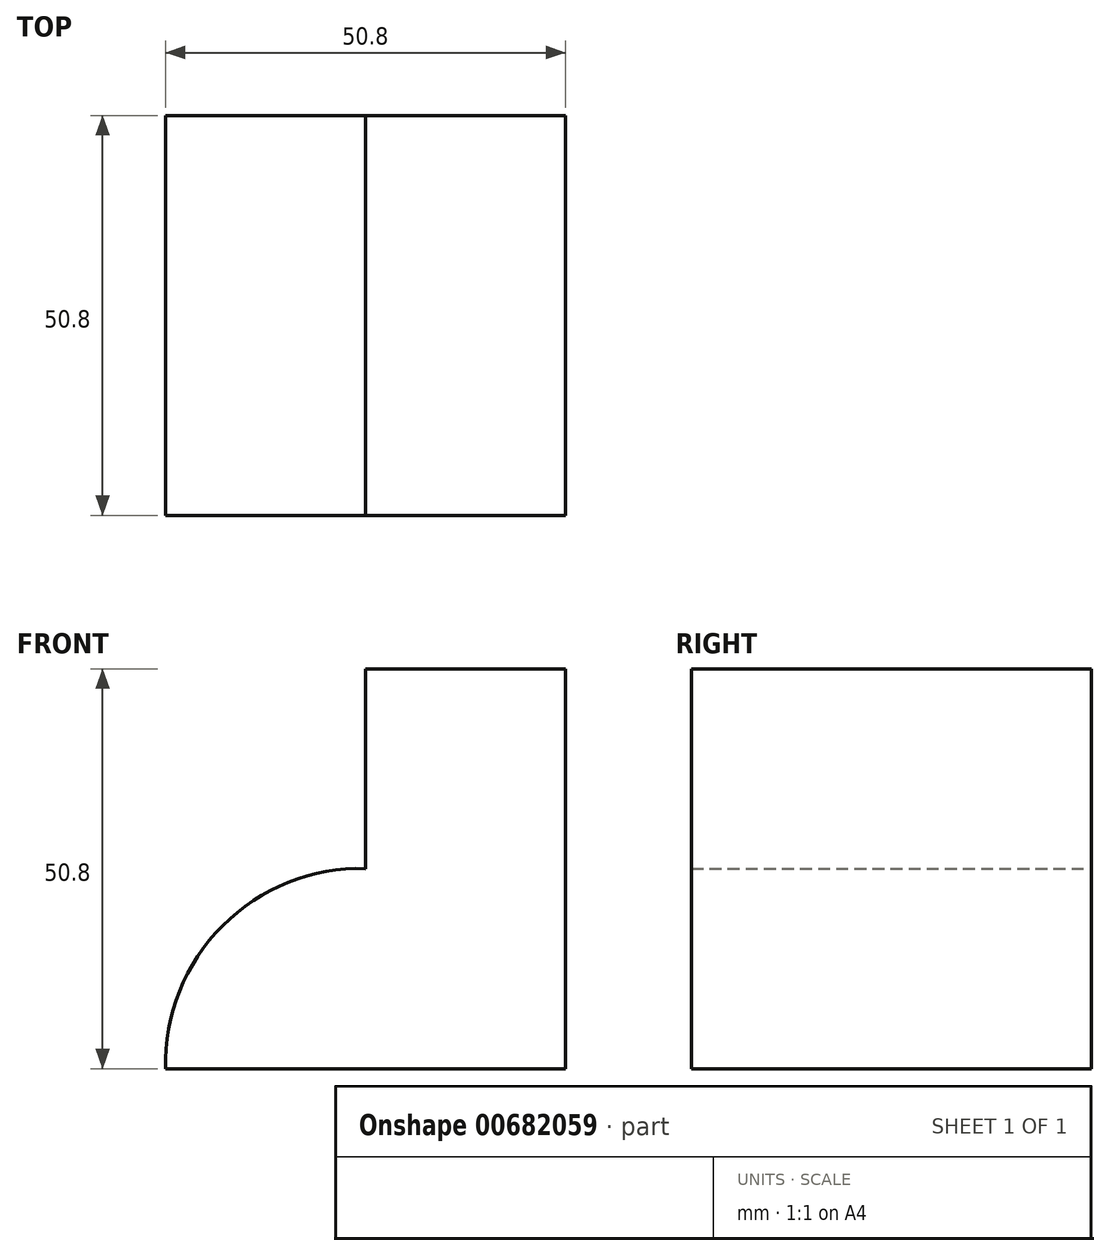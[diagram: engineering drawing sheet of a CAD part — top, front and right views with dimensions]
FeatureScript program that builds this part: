
annotation { "Feature Type Name" : "Feature", "Feature Type Description" : "" }
export const myFeature = defineFeature(function(context is Context, id is Id, definition is map)
    precondition{}
    {
        {
            var Q0;
            Q0=qCreatedBy(makeId("Front.planeOp"),FACE);
            var sketch = newSketch(context, id + "F0", { "sketchPlane" : qUnion([Q0])});
            skLineSegment(sketch, "E0", {"start": v(32.75, 36.57) * mm, "end": v(32.75, -14.23) * mm});
            skLineSegment(sketch, "E1", {"start": v(32.75, -14.23) * mm, "end": v(-18.05, -14.23) * mm});
            skLineSegment(sketch, "E2", {"start": v(32.75, 36.57) * mm, "end": v(7.35, 36.57) * mm});
            skLineSegment(sketch, "E3", {"start": v(7.35, 36.57) * mm, "end": v(7.35, 11.17) * mm});
            skArc(sketch, "E4", {"start": v(7.35, 11.17) * mm, "mid": v(-10.8, 3.93) * mm, "end": v(-18.05, -14.23) * mm});
            skSolve(sketch);
        }
        {
            var Q0;
            Q0 = qSketchRegion(id + "F0", true);
            extrude(context, id + "F1", {"entities" : qUnion([Q0]), "depth" : 50.8 * mm, "offsetDistance" : 25.4 * mm});
        }
    });
